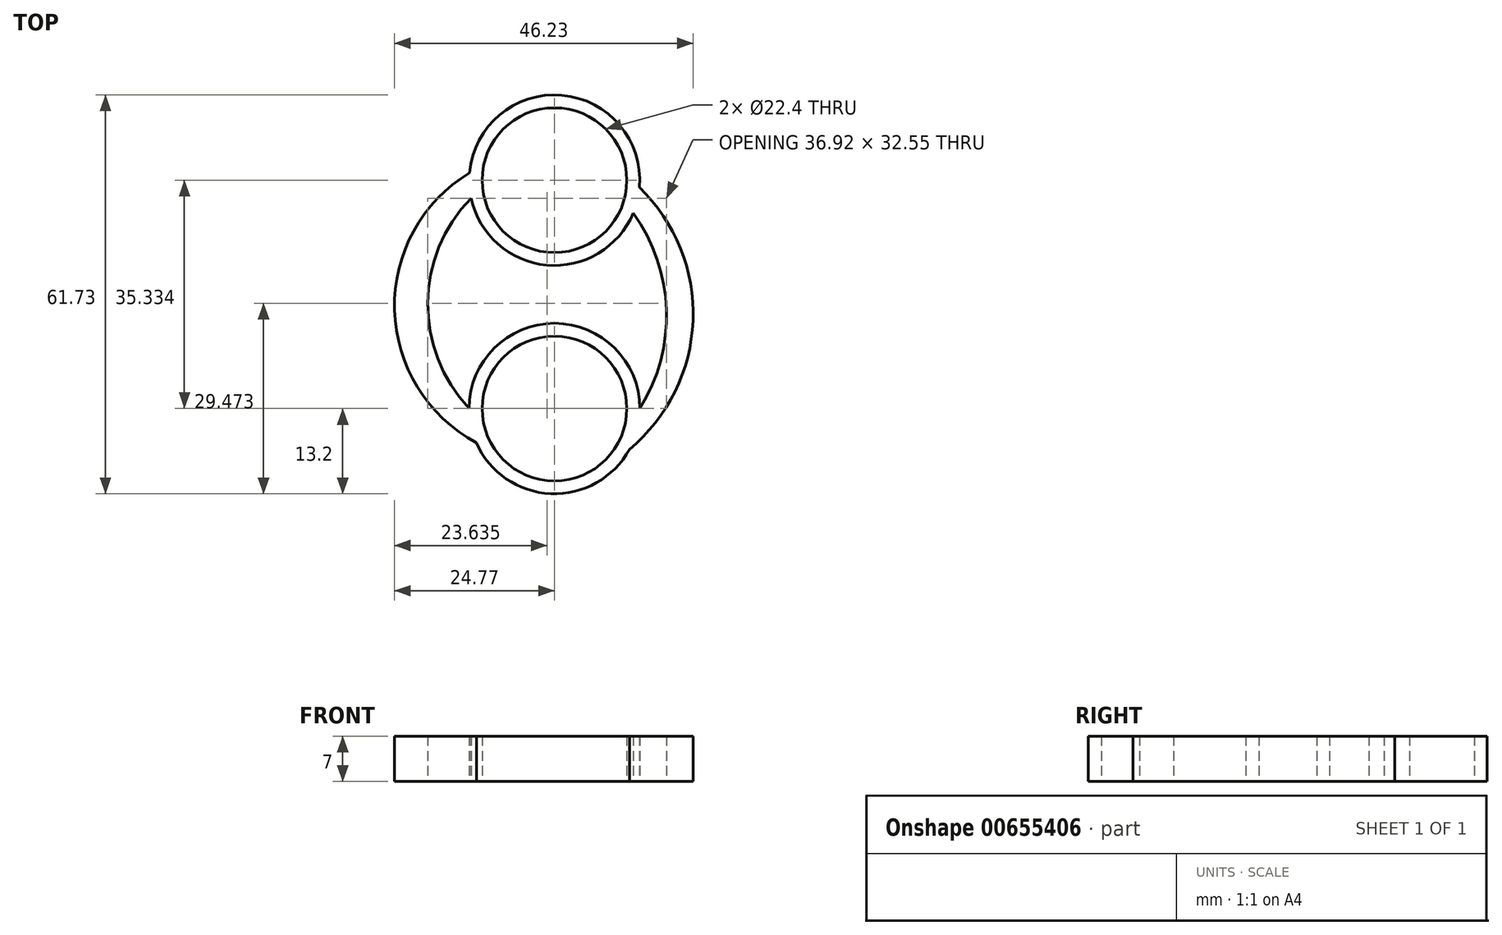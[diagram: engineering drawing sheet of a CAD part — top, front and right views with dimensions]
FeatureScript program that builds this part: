
annotation { "Feature Type Name" : "Feature", "Feature Type Description" : "" }
export const myFeature = defineFeature(function(context is Context, id is Id, definition is map)
    precondition{}
    {
        {
            var Q0;
            Q0=qCreatedBy(makeId("Top.planeOp"),FACE);
            var sketch = newSketch(context, id + "F0", { "sketchPlane" : qUnion([Q0])});
            skCircle(sketch, "E0", {"center": v(0, 0) * mm, "radius": 11.2 * mm});
            skCircle(sketch, "E1", {"center": v(0, 0) * mm, "radius": 13.2 * mm});
            skCircle(sketch, "E2", {"center": v(0, 35.33) * mm, "radius": 11.2 * mm});
            skCircle(sketch, "E3", {"center": v(0, 35.33) * mm, "radius": 13.2 * mm});
            skArc(sketch, "E4", {"start": v(13.2, 0) * mm, "mid": v(17.33, 15.27) * mm, "end": v(12.17, 30.23) * mm});
            skArc(sketch, "E5", {"start": v(11.6, -6.31) * mm, "mid": v(21.44, 13.6) * mm, "end": v(13.15, 34.22) * mm});
            skArc(sketch, "E6", {"start": v(-12.9, 32.55) * mm, "mid": v(-19.6, 16.33) * mm, "end": v(-13.2, 0) * mm});
            skArc(sketch, "E7", {"start": v(-13.15, 36.49) * mm, "mid": v(-24.76, 15.3) * mm, "end": v(-12.1, -5.29) * mm});
            skSolve(sketch);
        }
        {
            var Q0;
            Q0 = qSketchRegion(id + "F0", true);
            extrude(context, id + "F1", {"entities" : qUnion([Q0]), "depth" : 7 * mm, "offsetDistance" : 25 * mm});
        }
    });
